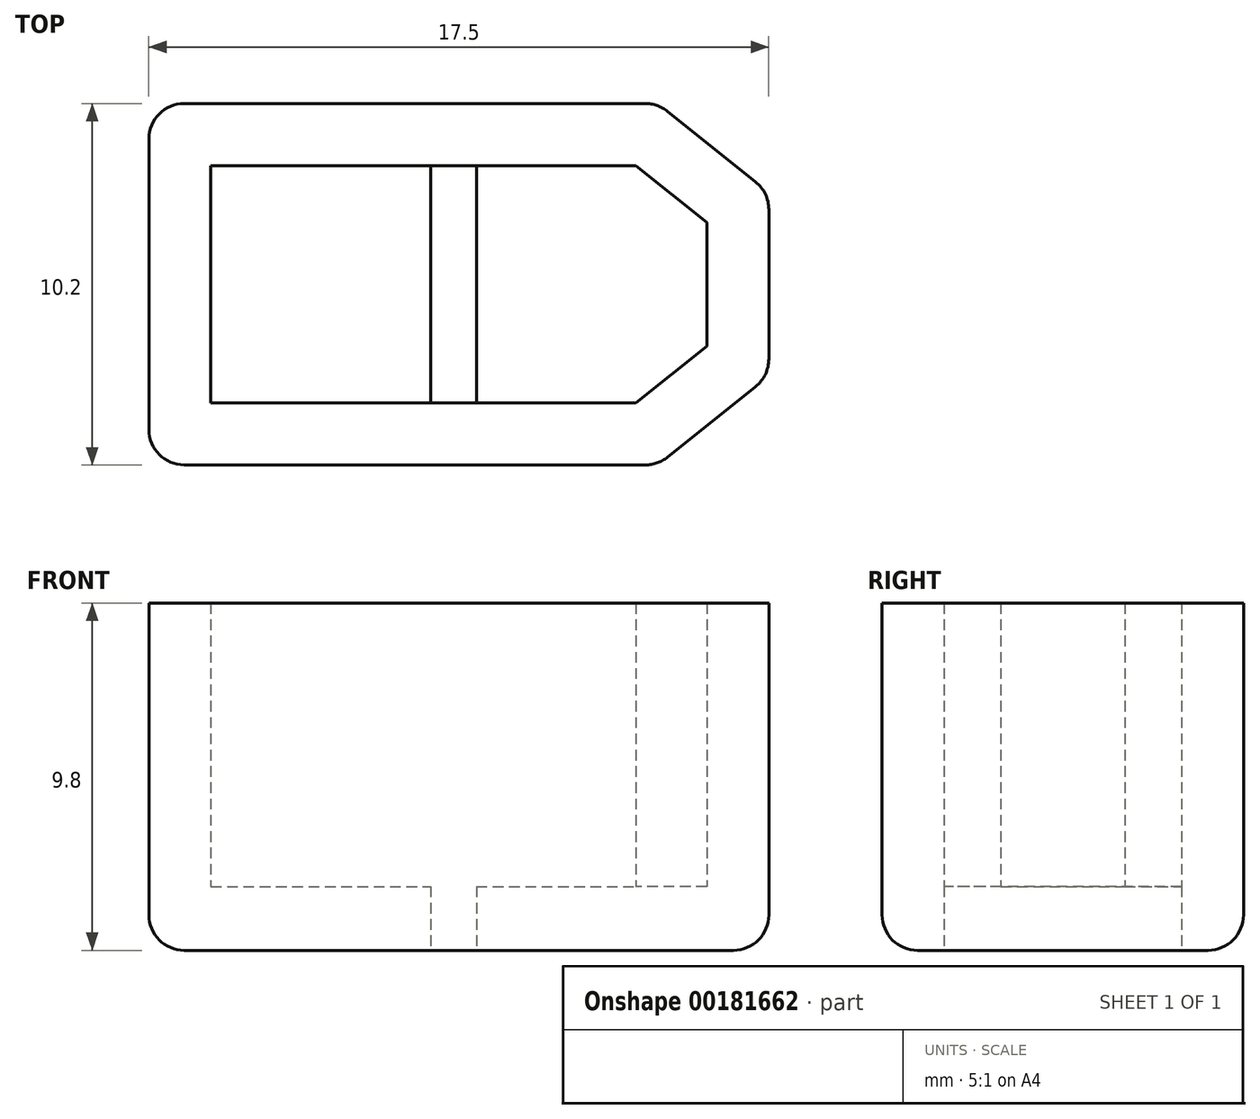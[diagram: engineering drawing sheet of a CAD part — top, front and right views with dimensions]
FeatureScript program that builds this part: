
annotation { "Feature Type Name" : "Feature", "Feature Type Description" : "" }
export const myFeature = defineFeature(function(context is Context, id is Id, definition is map)
    precondition{}
    {
        {
            var Q0;
            Q0=qCreatedBy(makeId("Top.planeOp"),FACE);
            var sketch = newSketch(context, id + "F0", { "sketchPlane" : qUnion([Q0])});
            skLineSegment(sketch, "E0", {"start": v(-8, 0) * mm, "end": v(-8, 3.35) * mm});
            skLineSegment(sketch, "E1", {"start": v(-8, 0) * mm, "end": v(6, 0) * mm});
            skLineSegment(sketch, "E2", {"start": v(-9.75, 0) * mm, "end": v(-9.75, 5.1) * mm});
            skLineSegment(sketch, "E3", {"start": v(7.75, 2.6) * mm, "end": v(7.75, 0) * mm});
            skLineSegment(sketch, "E4", {"start": v(-9.75, 0) * mm, "end": v(-8, 0) * mm});
            skLineSegment(sketch, "E5", {"start": v(6, 0) * mm, "end": v(7.75, 0) * mm});
            skLineSegment(sketch, "E6", {"start": v(6, 0) * mm, "end": v(6, 1.75) * mm});
            skLineSegment(sketch, "E7", {"start": v(6, 1.75) * mm, "end": v(4, 3.35) * mm});
            skLineSegment(sketch, "E8", {"start": v(-9.75, 5.1) * mm, "end": v(4.62, 5.1) * mm});
            skLineSegment(sketch, "E9", {"start": v(4.62, 5.1) * mm, "end": v(7.75, 2.6) * mm});
            skLineSegment(sketch, "E10", {"start": v(-8, 3.35) * mm, "end": v(4, 3.35) * mm});
            skLineSegment(sketch, "E11", {"start": v(-0.5, 3.35) * mm, "end": v(-0.5, 0) * mm});
            skLineSegment(sketch, "E12", {"start": v(-1.8, 3.35) * mm, "end": v(-1.8, 0) * mm});
            skSolve(sketch);
        }
        {
            var Q0;
            Q0=makeQuery(id+"F0.imprint","IMPRINT",FACE,{"disambiguationData":[TD([[makeQuery(id+"F0.imprint","IMPRINT",EDGE,{"derivedFrom":sQuery(id+"F0.wireOp",EDGE,"E0")}),-1.0]])]});
            var Q1;
            {var subQ3=sQuery(id+"F0.wireOp",EDGE,"E6");Q1=makeQuery(id+"F0.imprint","IMPRINT",FACE,{"disambiguationData":[TD([[makeQuery(id+"F0.imprint","IMPRINT",EDGE,{"derivedFrom":subQ3}),1.0]])]});}
            extrude(context, id + "F1", {"entities" : qUnion([Q0, Q1]), "depth" : 1.8 * mm});
        }
        {
            var Q0;
            Q0=makeQuery(id+"F0.imprint","IMPRINT",FACE,{"disambiguationData":[TD([[makeQuery(id+"F0.imprint","IMPRINT",EDGE,{"derivedFrom":sQuery(id+"F0.wireOp",EDGE,"E0")}),1.0]])]});
            extrude(context, id + "F2", {"entities" : qUnion([Q0]), "operationType" : NewBodyOperationType.ADD, "depth" : 9.8 * mm});
        }
        {
            var Q0;
            Q0=makeQuery(id+"F2.opExtrude","SWEPT_EDGE",EDGE,{"disambiguationData":[OSD([sQuery(id+"F0.wireOp",EDGE,"E2"),sQuery(id+"F0.wireOp",EDGE,"E8")])]});
            var Q1;
            Q1=makeQuery(id+"F2.opExtrude","SWEPT_EDGE",EDGE,{"disambiguationData":[OSD([sQuery(id+"F0.wireOp",EDGE,"E8"),sQuery(id+"F0.wireOp",EDGE,"E9")])]});
            var Q2;
            Q2=makeQuery(id+"F2.opExtrude","SWEPT_EDGE",EDGE,{"disambiguationData":[OSD([sQuery(id+"F0.wireOp",EDGE,"E3"),sQuery(id+"F0.wireOp",EDGE,"E9")])]});
            var Q3;
            Q3=makeQuery(id+"F2.opExtrude","CAP_EDGE",EDGE,{"disambiguationData":[OSD([sQuery(id+"F0.wireOp",EDGE,"E8")])],"isStart":true});
            var Q4;
            Q4=makeQuery(id+"F2.opExtrude","CAP_EDGE",EDGE,{"disambiguationData":[OSD([sQuery(id+"F0.wireOp",EDGE,"E9")])],"isStart":true});
            var Q5;
            Q5=makeQuery(id+"F2.opExtrude","CAP_EDGE",EDGE,{"disambiguationData":[OSD([sQuery(id+"F0.wireOp",EDGE,"E3")])],"isStart":true});
            var Q6;
            Q6=makeQuery(id+"F2.opExtrude","CAP_EDGE",EDGE,{"disambiguationData":[OSD([sQuery(id+"F0.wireOp",EDGE,"E2")])],"isStart":true});
            fillet(context, id + "F3", {"entities" : qUnion([Q0, Q1, Q2, Q3, Q4, Q5, Q6]), "radius" : 1 * mm, "tangentPropagation" : true, "allowEdgeOverflow" : false});
        }
        {
            var Q0;
            Q0=makeQuery(id+"F1.opExtrude","SWEPT_BODY",BODY,{"disambiguationData":[OSD([sQuery(id+"F0.wireOp",EDGE,"E0"),sQuery(id+"F0.wireOp",EDGE,"E1"),sQuery(id+"F0.wireOp",EDGE,"E10"),sQuery(id+"F0.wireOp",EDGE,"E12")])]});
            var Q1;
            Q1=makeQuery(id+"F2.boolean.opBoolean","MERGE",FACE,{"derivedFrom":[makeQuery(id+"F1.opExtrude","SWEPT_FACE",FACE,{"disambiguationData":[OSD([sQuery(id+"F0.wireOp",EDGE,"E1")])]}),makeQuery(id+"F2.opExtrude","SWEPT_FACE",FACE,{"disambiguationData":[OSD([sQuery(id+"F0.wireOp",EDGE,"E4")])]}),makeQuery(id+"F2.opExtrude","SWEPT_FACE",FACE,{"disambiguationData":[OSD([sQuery(id+"F0.wireOp",EDGE,"E5")])]})]});
            mirror(context, id + "F4", {"operationType" : NewBodyOperationType.ADD, "entities" : qUnion([Q0]), "mirrorPlane" : qUnion([Q1])});
        }
    });
